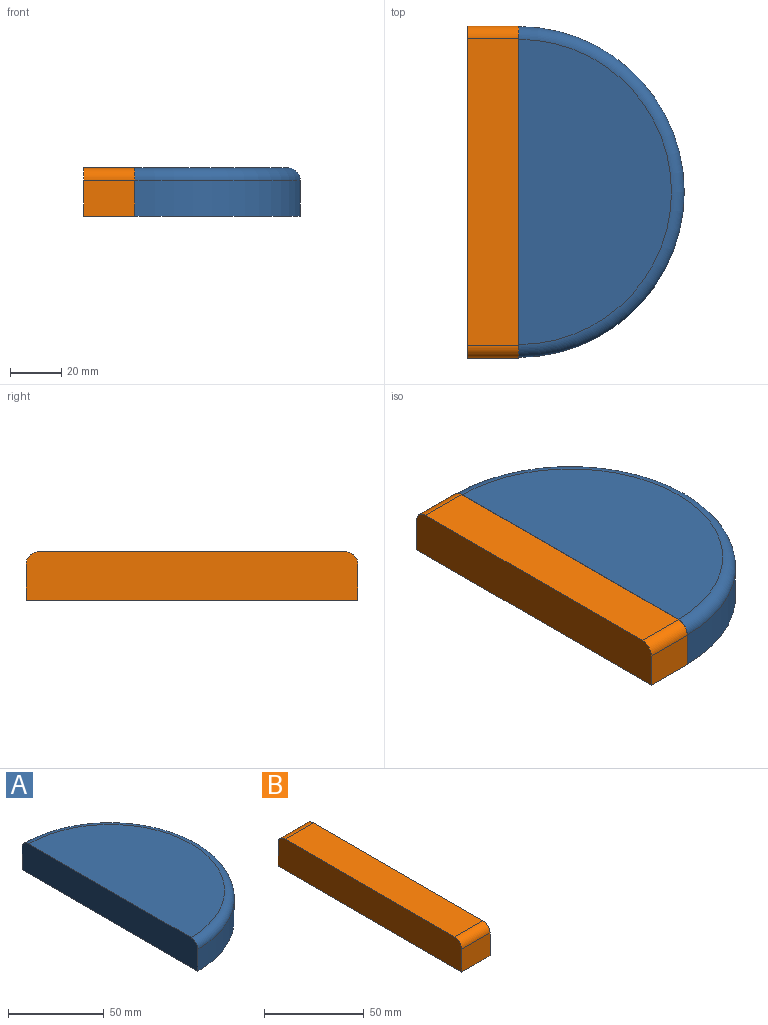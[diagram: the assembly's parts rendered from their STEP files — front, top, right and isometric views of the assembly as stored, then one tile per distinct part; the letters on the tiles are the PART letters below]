
ASSEMBLY  parts=2 mates=1
PART A: 5 faces, bbox 70.1x140.2x19 mm
  f0: plane 129.54x19mm, normal (-1,0,0), area 2450.4mm2, adj f1,f2,f3,f4
  f1: cylinder r=64.77mm len=129.54mm, axis (0,0,-1), area 2848.6mm2, adj f0,f3,f4
  f2: plane 119.54x59.77mm, normal (0,0,1), area 5611.2mm2, adj f0,f4
  f3: plane 129.54x64.77mm, normal (0,0,-1), area 6589.3mm2, adj f0,f1
  f4: torus R=59.77mm, axis (0,0,1), area 1553.3mm2, adj f0,f1,f2
PART B: 8 faces, bbox 20x130x19 mm
  f0: plane 20x14mm, normal (0,1,0), area 280mm2, adj f1,f3,f5,f7
  f1: plane 130x19mm, normal (-1,0,0), area 2459.3mm2, adj f0,f2,f4,f5,f6,f7
  f2: plane 20x14mm, normal (0,-1,0), area 280mm2, adj f1,f3,f5,f6
  f3: plane 130x19mm, normal (1,0,0), area 2459.3mm2, adj f0,f2,f4,f5,f6,f7
  f4: plane 120x20mm, normal (0,0,1), area 2400mm2, adj f1,f3,f6,f7
  f5: plane 130x20mm, normal (0,0,-1), area 2600mm2, adj f0,f1,f2,f3
  f6: cylinder r=5mm len=20mm, axis (-1,0,0), area 157.1mm2, adj f1,f2,f3,f4
  f7: cylinder r=5mm len=20mm, axis (1,0,0), area 157.1mm2, adj f0,f1,f3,f4
PLACE A t=(78.93,-20.02,1.89)mm
PLACE B t=(152.41,-47.93,1.89)mm
MATE parallel B.f3 <-> A.f0  axis (1,0,0) through (78.93,-20.02,11.35)mm
